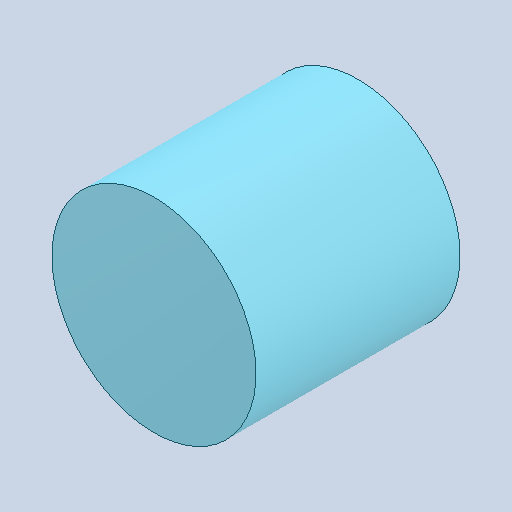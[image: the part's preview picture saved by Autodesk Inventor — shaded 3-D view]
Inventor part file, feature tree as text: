
AUTODESK INVENTOR PART (.ipt)
format: ipt  version: 2022 (Build 260153000, 153)  size: 96,256 bytes
history: imported  units: in
note: dims shown in document units (in); Inventor stores cm internally (conversion verified against a paired STEP export)
features: imported_body x1
ambient origin geometry x8: Origin, YZ Plane, XZ Plane, XY Plane, X Axis, Y Axis, Z Axis, Center Point
bodies: Solid1 (imported_parasolid), Body1 (imported_parasolid)
feature tree (1):
  imported_body  NMx_Import_Brep_tag  [imported B-rep: ~3 faces, bbox_mm=[5.593965, 3.005005, 6.35]]
